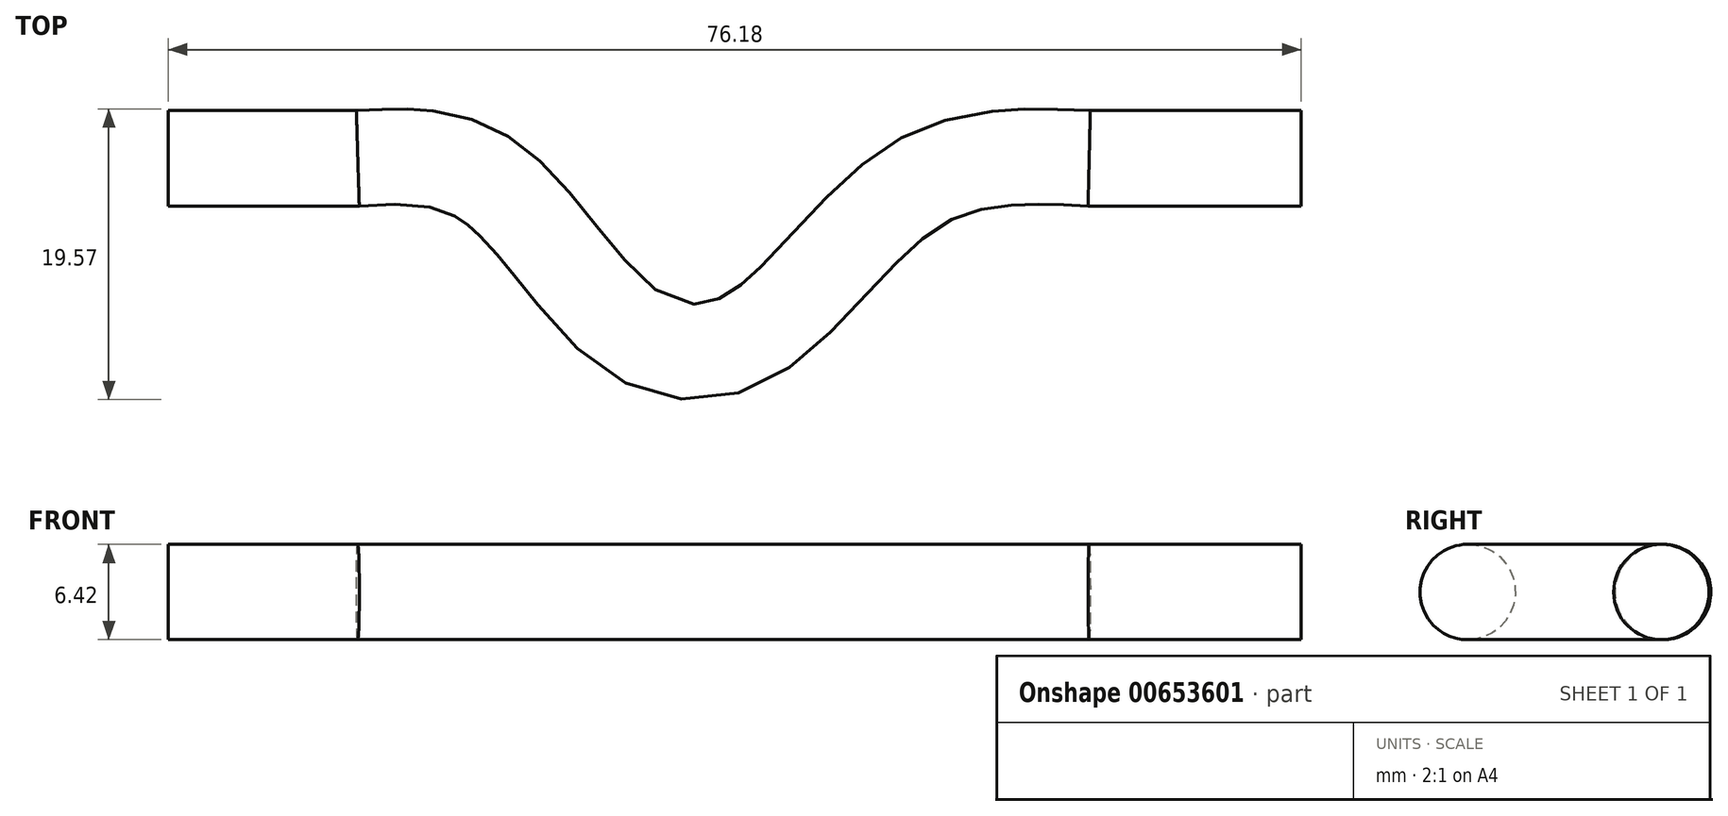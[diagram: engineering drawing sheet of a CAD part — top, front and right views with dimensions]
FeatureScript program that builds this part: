
annotation { "Feature Type Name" : "Feature", "Feature Type Description" : "" }
export const myFeature = defineFeature(function(context is Context, id is Id, definition is map)
    precondition{}
    {
        {
            var Q0;
            Q0=qCreatedBy(makeId("Top.planeOp"),FACE);
            var sketch = newSketch(context, id + "F0", { "sketchPlane" : qUnion([Q0])});
            skLineSegment(sketch, "E0", {"start": v(-76.18, 0) * mm, "end": v(-63.44, 0) * mm});
            skFitSpline(sketch, "E1", {"points": [v(-63.44, 0) * mm, v(-54.77, -1.43) * mm, v(-45.21, -11.52) * mm, v(-36.9, -11.87) * mm, v(-25.92, -1.78) * mm, v(-14.25, 0) * mm], "startDerivative": vector(51.27, 3.13) * mm, "endDerivative": vector(59.92, -2.86) * mm});
            skLineSegment(sketch, "E2", {"start": v(-14.25, 0) * mm, "end": v(0, 0) * mm});
            skSolve(sketch);
        }
        {
            var Q0;
            Q0=qCreatedBy(makeId("Right.planeOp"),FACE);
            var sketch = newSketch(context, id + "F1", { "sketchPlane" : qUnion([Q0])});
            skCircle(sketch, "E3", {"center": v(0, 0) * mm, "radius": 3.21 * mm});
            skSolve(sketch);
        }
        {
            var Q0;
            Q0 = qSketchRegion(id + "F1", true);
            var Q1;
            Q1=sQuery(id+"F0.wireOp",EDGE,"E2");
            var Q2;
            Q2=sQuery(id+"F0.wireOp",EDGE,"E1");
            var Q3;
            Q3=sQuery(id+"F0.wireOp",EDGE,"E0");
            sweep(context, id + "F2", {"profiles" : qUnion([Q0]), "path" : qUnion([Q1, Q2, Q3])});
        }
    });
